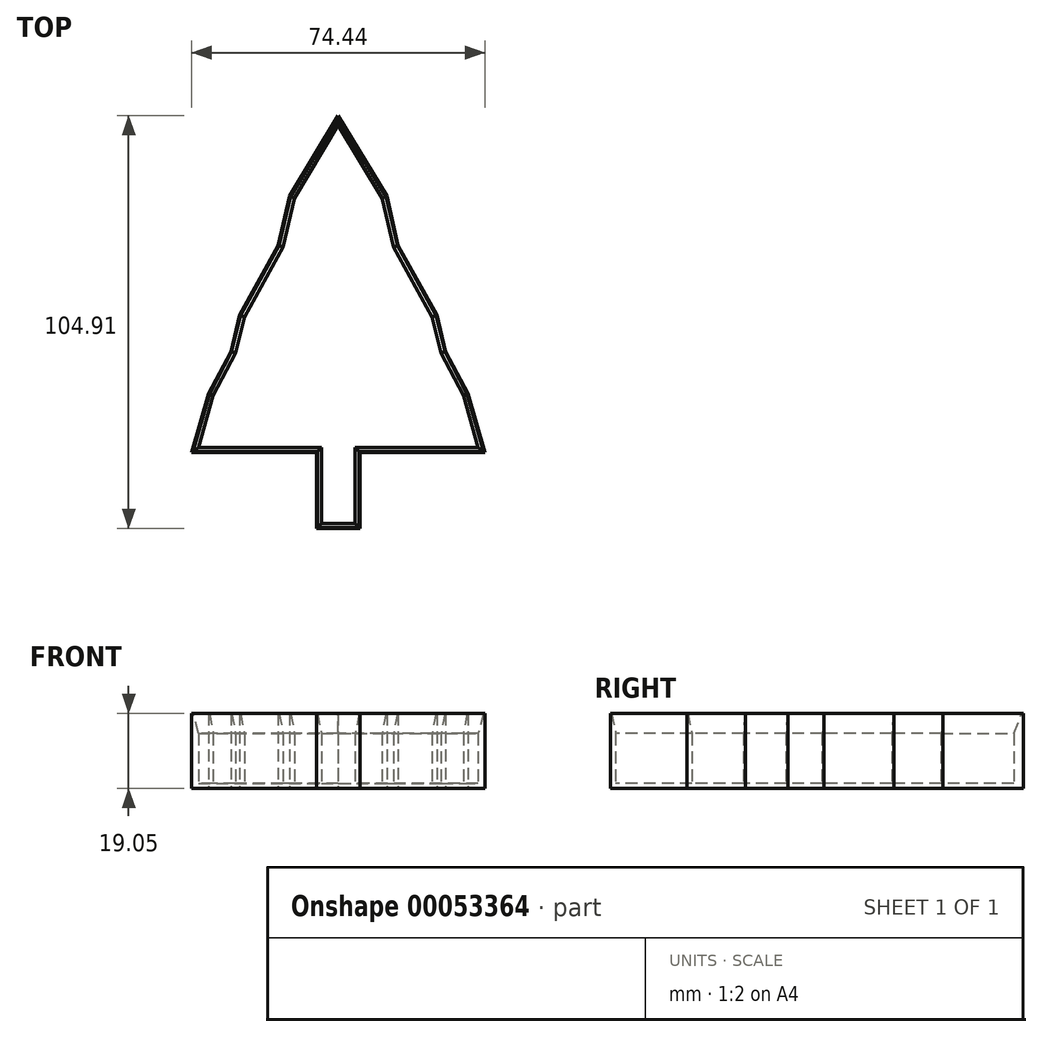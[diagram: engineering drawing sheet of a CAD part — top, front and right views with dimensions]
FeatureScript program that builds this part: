
annotation { "Feature Type Name" : "Feature", "Feature Type Description" : "" }
export const myFeature = defineFeature(function(context is Context, id is Id, definition is map)
    precondition{}
    {
        {
            var Q0;
            Q0=qCreatedBy(makeId("Top.planeOp"),FACE);
            var sketch = newSketch(context, id + "F0", { "sketchPlane" : qUnion([Q0])});
            skLineSegment(sketch, "E0", {"start": v(0, 48.35) * mm, "end": v(12.33, 27.86) * mm});
            skLineSegment(sketch, "E1", {"start": v(12.33, 27.86) * mm, "end": v(15.24, 15.35) * mm});
            skLineSegment(sketch, "E2", {"start": v(15.24, 15.35) * mm, "end": v(25.05, -2.38) * mm});
            skLineSegment(sketch, "E3", {"start": v(25.05, -2.38) * mm, "end": v(27.3, -11.55) * mm});
            skLineSegment(sketch, "E4", {"start": v(27.3, -11.55) * mm, "end": v(32.95, -22.33) * mm});
            skLineSegment(sketch, "E5", {"start": v(32.95, -22.33) * mm, "end": v(37.22, -37.22) * mm});
            skLineSegment(sketch, "E6", {"start": v(37.22, -37.22) * mm, "end": v(5.56, -37.22) * mm});
            skLineSegment(sketch, "E7", {"start": v(5.56, -37.22) * mm, "end": v(5.56, -56.56) * mm});
            skLineSegment(sketch, "E8", {"start": v(5.56, -56.56) * mm, "end": v(0, -56.56) * mm});
            skLineSegment(sketch, "E9.MirrorCS", {"start": v(0, 48.35) * mm, "end": v(-12.33, 27.86) * mm});
            skLineSegment(sketch, "E10.MirrorCS", {"start": v(-12.33, 27.86) * mm, "end": v(-15.24, 15.35) * mm});
            skLineSegment(sketch, "E11.MirrorCS", {"start": v(-15.24, 15.35) * mm, "end": v(-25.05, -2.38) * mm});
            skLineSegment(sketch, "E12.MirrorCS", {"start": v(-25.05, -2.38) * mm, "end": v(-27.3, -11.55) * mm});
            skLineSegment(sketch, "E13.MirrorCS", {"start": v(-27.3, -11.55) * mm, "end": v(-32.95, -22.33) * mm});
            skLineSegment(sketch, "E14.MirrorCS", {"start": v(-32.95, -22.33) * mm, "end": v(-37.22, -37.22) * mm});
            skLineSegment(sketch, "E15.MirrorCS", {"start": v(-37.22, -37.22) * mm, "end": v(-5.56, -37.22) * mm});
            skLineSegment(sketch, "E16.MirrorCS", {"start": v(-5.56, -56.56) * mm, "end": v(0, -56.56) * mm});
            skLineSegment(sketch, "E17.MirrorCS", {"start": v(-5.56, -37.22) * mm, "end": v(-5.56, -56.56) * mm});
            skSolve(sketch);
        }
        {
            var Q0;
            Q0=makeQuery(id+"F0.imprint","IMPRINT",FACE,{"disambiguationData":[TD([[makeQuery(id+"F0.imprint","IMPRINT",EDGE,{"derivedFrom":sQuery(id+"F0.wireOp",EDGE,"E0")}),-1.0]])]});
            extrude(context, id + "F1", {"entities" : qUnion([Q0]), "depth" : 19.05 * mm});
        }
        {
            var Q0;
            Q0=makeQuery(id+"F1.opExtrude","CAP_FACE",FACE,{"disambiguationData":[OSD([sQuery(id+"F0.wireOp",EDGE,"E0"),sQuery(id+"F0.wireOp",EDGE,"E1"),sQuery(id+"F0.wireOp",EDGE,"E2"),sQuery(id+"F0.wireOp",EDGE,"E3"),sQuery(id+"F0.wireOp",EDGE,"E4"),sQuery(id+"F0.wireOp",EDGE,"E5"),sQuery(id+"F0.wireOp",EDGE,"E6"),sQuery(id+"F0.wireOp",EDGE,"E7"),sQuery(id+"F0.wireOp",EDGE,"E8"),sQuery(id+"F0.wireOp",EDGE,"E9.MirrorCS"),sQuery(id+"F0.wireOp",EDGE,"E10.MirrorCS"),sQuery(id+"F0.wireOp",EDGE,"E11.MirrorCS"),sQuery(id+"F0.wireOp",EDGE,"E12.MirrorCS"),sQuery(id+"F0.wireOp",EDGE,"E13.MirrorCS"),sQuery(id+"F0.wireOp",EDGE,"E14.MirrorCS"),sQuery(id+"F0.wireOp",EDGE,"E15.MirrorCS"),sQuery(id+"F0.wireOp",EDGE,"E16.MirrorCS"),sQuery(id+"F0.wireOp",EDGE,"E17.MirrorCS")])],"isStart":false});
            shell(context, id + "F2", {"entities" : qUnion([Q0]), "thickness" : 1.27 * mm});
        }
        {
            var Q0;
            {var subQ0=sQuery(id+"F0.wireOp",EDGE,"E7");Q0=makeQuery(id+"F2.opShell","OFFSET_EDGE",EDGE,{"disambiguationData":[OSD([subQ0]),TDD([makeQuery(id+"F1.opExtrude","CAP_EDGE",EDGE,{"disambiguationData":[OSD([subQ0])],"isStart":false})])]});}
            var Q1;
            {var subQ0=sQuery(id+"F0.wireOp",EDGE,"E6");Q1=makeQuery(id+"F2.opShell","OFFSET_EDGE",EDGE,{"disambiguationData":[OSD([subQ0]),TDD([makeQuery(id+"F1.opExtrude","CAP_EDGE",EDGE,{"disambiguationData":[OSD([subQ0])],"isStart":false})])]});}
            var Q2;
            {var subQ0=sQuery(id+"F0.wireOp",EDGE,"E17.MirrorCS");Q2=makeQuery(id+"F2.opShell","OFFSET_EDGE",EDGE,{"disambiguationData":[OSD([subQ0]),TDD([makeQuery(id+"F1.opExtrude","CAP_EDGE",EDGE,{"disambiguationData":[OSD([subQ0])],"isStart":false})])]});}
            var Q3;
            {var subQ0=sQuery(id+"F0.wireOp",EDGE,"E16.MirrorCS");var subQ1=sQuery(id+"F0.wireOp",EDGE,"E8");Q3=makeQuery(id+"F2.opShell","OFFSET_EDGE",EDGE,{"disambiguationData":[OSD([subQ1,subQ0]),TDD([makeQuery(id+"F1.opExtrude","CAP_EDGE",EDGE,{"disambiguationData":[OSD([subQ1,subQ0])],"isStart":false})])]});}
            var Q4;
            {var subQ0=sQuery(id+"F0.wireOp",EDGE,"E15.MirrorCS");Q4=makeQuery(id+"F2.opShell","OFFSET_EDGE",EDGE,{"disambiguationData":[OSD([subQ0]),TDD([makeQuery(id+"F1.opExtrude","CAP_EDGE",EDGE,{"disambiguationData":[OSD([subQ0])],"isStart":false})])]});}
            var Q5;
            {var subQ0=sQuery(id+"F0.wireOp",EDGE,"E5");Q5=makeQuery(id+"F2.opShell","OFFSET_EDGE",EDGE,{"disambiguationData":[OSD([subQ0]),TDD([makeQuery(id+"F1.opExtrude","CAP_EDGE",EDGE,{"disambiguationData":[OSD([subQ0])],"isStart":false})])]});}
            var Q6;
            {var subQ0=sQuery(id+"F0.wireOp",EDGE,"E4");Q6=makeQuery(id+"F2.opShell","OFFSET_EDGE",EDGE,{"disambiguationData":[OSD([subQ0]),TDD([makeQuery(id+"F1.opExtrude","CAP_EDGE",EDGE,{"disambiguationData":[OSD([subQ0])],"isStart":false})])]});}
            var Q7;
            {var subQ0=sQuery(id+"F0.wireOp",EDGE,"E3");Q7=makeQuery(id+"F2.opShell","OFFSET_EDGE",EDGE,{"disambiguationData":[OSD([subQ0]),TDD([makeQuery(id+"F1.opExtrude","CAP_EDGE",EDGE,{"disambiguationData":[OSD([subQ0])],"isStart":false})])]});}
            var Q8;
            {var subQ0=sQuery(id+"F0.wireOp",EDGE,"E2");Q8=makeQuery(id+"F2.opShell","OFFSET_EDGE",EDGE,{"disambiguationData":[OSD([subQ0]),TDD([makeQuery(id+"F1.opExtrude","CAP_EDGE",EDGE,{"disambiguationData":[OSD([subQ0])],"isStart":false})])]});}
            var Q9;
            {var subQ0=sQuery(id+"F0.wireOp",EDGE,"E1");Q9=makeQuery(id+"F2.opShell","OFFSET_EDGE",EDGE,{"disambiguationData":[OSD([subQ0]),TDD([makeQuery(id+"F1.opExtrude","CAP_EDGE",EDGE,{"disambiguationData":[OSD([subQ0])],"isStart":false})])]});}
            var Q10;
            {var subQ0=sQuery(id+"F0.wireOp",EDGE,"E0");Q10=makeQuery(id+"F2.opShell","OFFSET_EDGE",EDGE,{"disambiguationData":[OSD([subQ0]),TDD([makeQuery(id+"F1.opExtrude","CAP_EDGE",EDGE,{"disambiguationData":[OSD([subQ0])],"isStart":false})])]});}
            var Q11;
            {var subQ0=sQuery(id+"F0.wireOp",EDGE,"E9.MirrorCS");Q11=makeQuery(id+"F2.opShell","OFFSET_EDGE",EDGE,{"disambiguationData":[OSD([subQ0]),TDD([makeQuery(id+"F1.opExtrude","CAP_EDGE",EDGE,{"disambiguationData":[OSD([subQ0])],"isStart":false})])]});}
            var Q12;
            {var subQ0=sQuery(id+"F0.wireOp",EDGE,"E10.MirrorCS");Q12=makeQuery(id+"F2.opShell","OFFSET_EDGE",EDGE,{"disambiguationData":[OSD([subQ0]),TDD([makeQuery(id+"F1.opExtrude","CAP_EDGE",EDGE,{"disambiguationData":[OSD([subQ0])],"isStart":false})])]});}
            var Q13;
            {var subQ0=sQuery(id+"F0.wireOp",EDGE,"E11.MirrorCS");Q13=makeQuery(id+"F2.opShell","OFFSET_EDGE",EDGE,{"disambiguationData":[OSD([subQ0]),TDD([makeQuery(id+"F1.opExtrude","CAP_EDGE",EDGE,{"disambiguationData":[OSD([subQ0])],"isStart":false})])]});}
            var Q14;
            {var subQ0=sQuery(id+"F0.wireOp",EDGE,"E12.MirrorCS");Q14=makeQuery(id+"F2.opShell","OFFSET_EDGE",EDGE,{"disambiguationData":[OSD([subQ0]),TDD([makeQuery(id+"F1.opExtrude","CAP_EDGE",EDGE,{"disambiguationData":[OSD([subQ0])],"isStart":false})])]});}
            var Q15;
            {var subQ0=sQuery(id+"F0.wireOp",EDGE,"E13.MirrorCS");Q15=makeQuery(id+"F2.opShell","OFFSET_EDGE",EDGE,{"disambiguationData":[OSD([subQ0]),TDD([makeQuery(id+"F1.opExtrude","CAP_EDGE",EDGE,{"disambiguationData":[OSD([subQ0])],"isStart":false})])]});}
            var Q16;
            {var subQ0=sQuery(id+"F0.wireOp",EDGE,"E14.MirrorCS");Q16=makeQuery(id+"F2.opShell","OFFSET_EDGE",EDGE,{"disambiguationData":[OSD([subQ0]),TDD([makeQuery(id+"F1.opExtrude","CAP_EDGE",EDGE,{"disambiguationData":[OSD([subQ0])],"isStart":false})])]});}
            chamfer(context, id + "F3", {"entities" : qUnion([Q0, Q1, Q2, Q3, Q4, Q5, Q6, Q7, Q8, Q9, Q10, Q11, Q12, Q13, Q14, Q15, Q16]), "chamferType" : ChamferType.TWO_OFFSETS, "width1" : 1.02 * mm, "oppositeDirection" : false, "width2" : 5.08 * mm, "tangentPropagation" : true});
        }
    });
